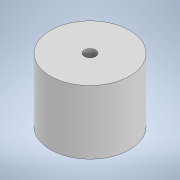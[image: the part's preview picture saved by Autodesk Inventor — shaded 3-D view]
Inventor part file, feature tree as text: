
AUTODESK INVENTOR PART (.ipt)
format: ipt  version: 2020 (Build 240168000, 168)  size: 96,768 bytes
history: native  units: mm
features: extrude x2, sketch x2
ambient origin geometry x8: Origin, YZ Plane, XZ Plane, XY Plane, X Axis, Y Axis, Z Axis, Center Point
bodies: Solid1 (feature_tree)
feature tree (4):
  extrude  "Extrusion1"  Depth=22.5mm TaperAngle=0.0deg
  extrude  "Extrusion2"  Depth=10.0mm TaperAngle=0.0deg
  sketch  "Sketch1"  dims[d0=28.0mm d1=22.5mm d2=0.0mm]
  sketch  "Sketch2"  dims[d3=4.0mm d4=10.0mm d5=0.0mm]
